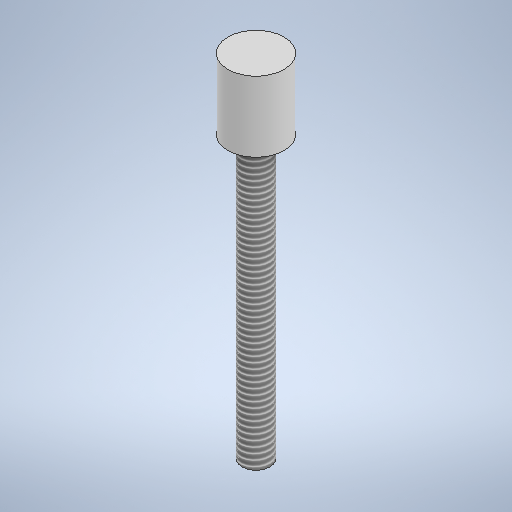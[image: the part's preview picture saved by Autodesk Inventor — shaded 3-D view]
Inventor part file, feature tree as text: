
AUTODESK INVENTOR PART (.ipt)
format: ipt  version: 2025.2 (Build 292293000, 293)  size: 263,680 bytes
history: native  units: mm
features: extrude x2, sketch x2, other x1, thread x1
ambient origin geometry x8: Origin, YZ Plane, XZ Plane, XY Plane, X Axis, Y Axis, Z Axis, Center Point
bodies: Body1 (feature_tree)
feature tree (6):
  other  "Bryła1"
  extrude  "Wyciągnięcie proste1"  Depth=4.0mm
  extrude  "Wyciągnięcie proste2"  Depth=5.0mm TaperAngle=0.0deg
  thread  "Gwint1"
  sketch  "Szkic1"
  sketch  "Szkic2"
